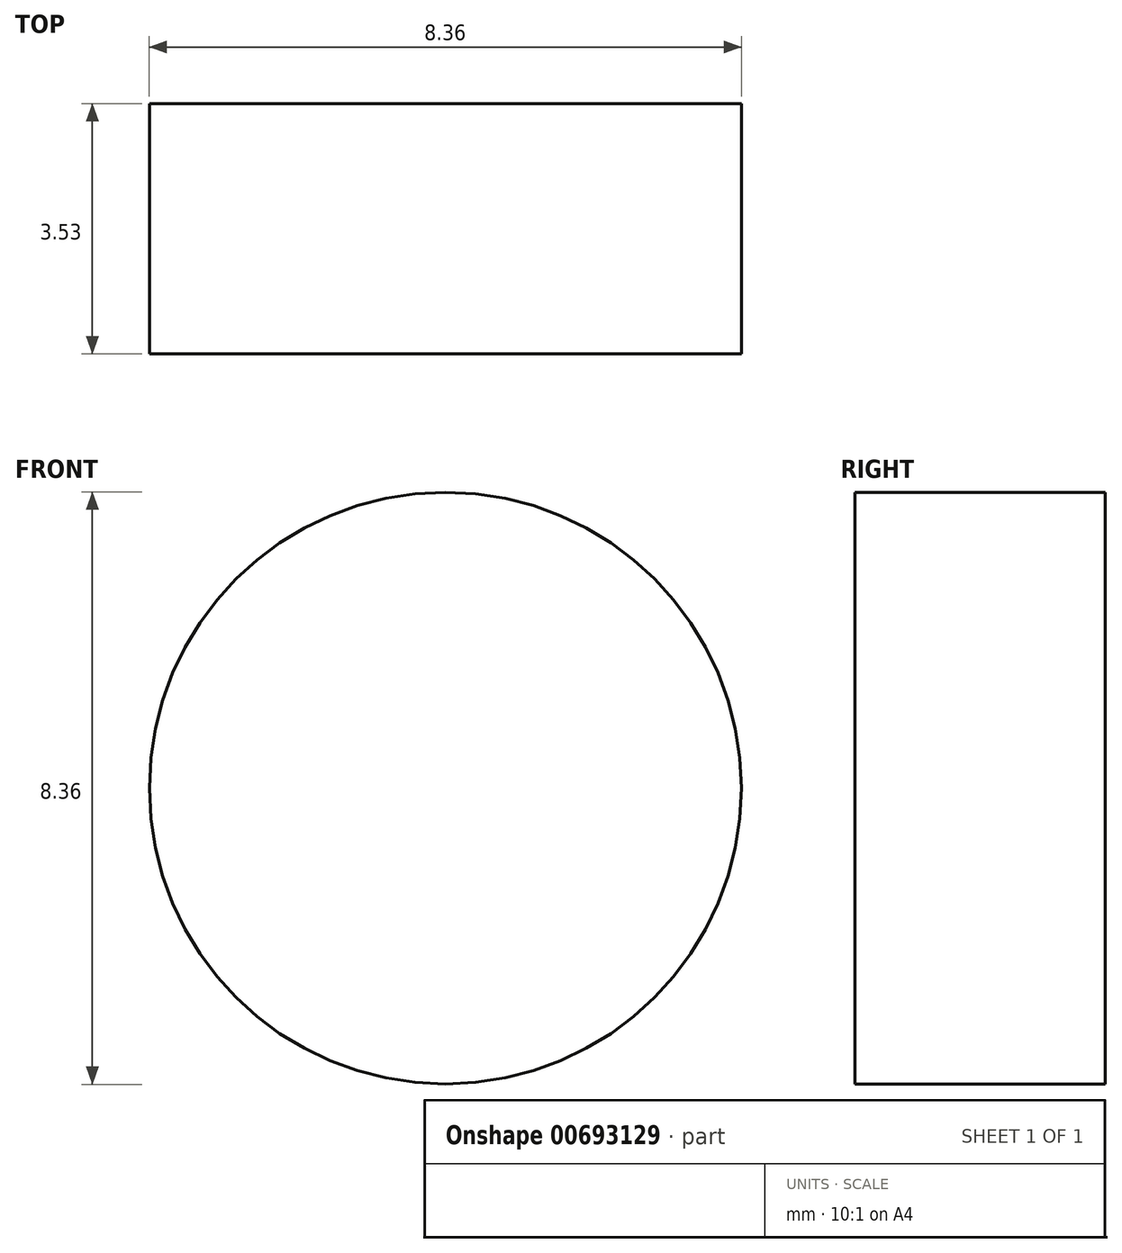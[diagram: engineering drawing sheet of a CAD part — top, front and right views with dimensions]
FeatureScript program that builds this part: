
annotation { "Feature Type Name" : "Feature", "Feature Type Description" : "" }
export const myFeature = defineFeature(function(context is Context, id is Id, definition is map)
    precondition{}
    {
        {
            var Q0;
            Q0=qCreatedBy(makeId("Front.planeOp"),FACE);
            var sketch = newSketch(context, id + "F0", { "sketchPlane" : qUnion([Q0])});
            skCircle(sketch, "E0", {"center": v(0, 0) * mm, "radius": 4.18 * mm});
            skSolve(sketch);
        }
        {
            var Q0;
            Q0=makeQuery(id+"F0.imprint","IMPRINT",FACE,{"disambiguationData":[TD([[makeQuery(id+"F0.imprint","IMPRINT",EDGE,{"derivedFrom":sQuery(id+"F0.wireOp",EDGE,"E0")}),1.0]])]});
            extrude(context, id + "F1", {"entities" : qUnion([Q0]), "depth" : 3.53 * mm, "offsetDistance" : 25 * mm});
        }
    });
